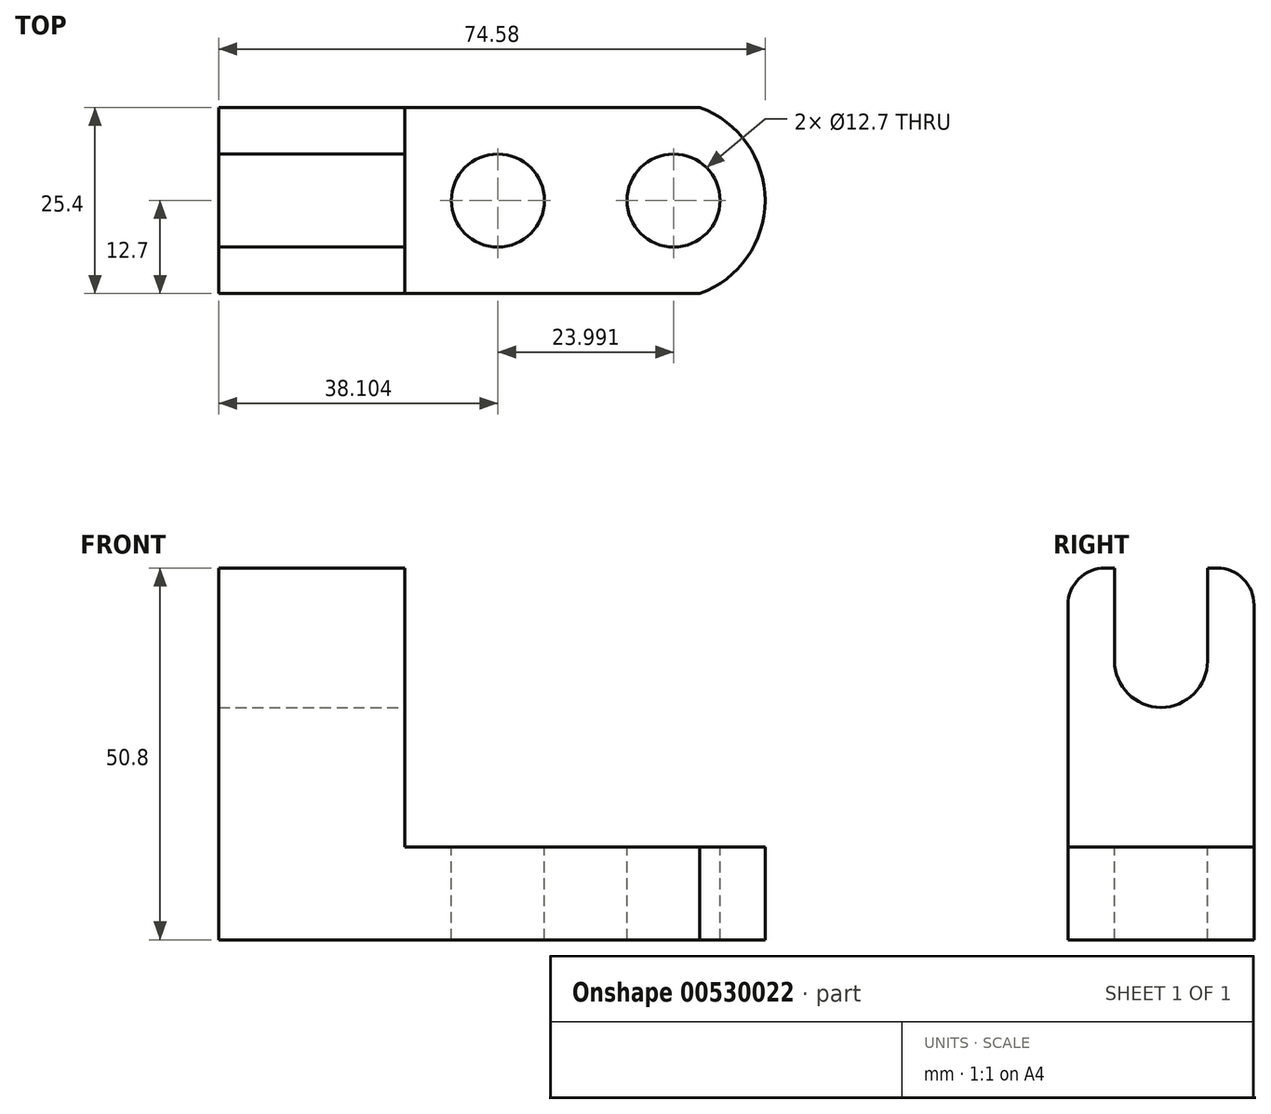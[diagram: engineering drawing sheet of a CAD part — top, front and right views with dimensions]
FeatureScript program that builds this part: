
annotation { "Feature Type Name" : "Feature", "Feature Type Description" : "" }
export const myFeature = defineFeature(function(context is Context, id is Id, definition is map)
    precondition{}
    {
        {
            var Q0;
            Q0=qCreatedBy(makeId("Front.planeOp"),FACE);
            var sketch = newSketch(context, id + "F0", { "sketchPlane" : qUnion([Q0])});
            skLineSegment(sketch, "E0", {"start": v(-65.68, 60.9) * mm, "end": v(-65.68, 10.1) * mm});
            skLineSegment(sketch, "E1", {"start": v(-65.68, 10.1) * mm, "end": v(9.11, 10.1) * mm});
            skLineSegment(sketch, "E2", {"start": v(9.11, 10.1) * mm, "end": v(9.11, 22.8) * mm});
            skLineSegment(sketch, "E3", {"start": v(9.11, 22.8) * mm, "end": v(-40.28, 22.8) * mm});
            skLineSegment(sketch, "E4", {"start": v(-40.28, 22.8) * mm, "end": v(-40.28, 60.9) * mm});
            skLineSegment(sketch, "E5", {"start": v(-65.68, 60.9) * mm, "end": v(-40.28, 60.9) * mm});
            skSolve(sketch);
        }
        {
            var Q0;
            Q0=makeQuery(id+"F0.imprint","IMPRINT",FACE,{"disambiguationData":[TD([[makeQuery(id+"F0.imprint","IMPRINT",EDGE,{"derivedFrom":sQuery(id+"F0.wireOp",EDGE,"E0")}),1.0]])]});
            extrude(context, id + "F1", {"entities" : qUnion([Q0]), "depth" : 25.4 * mm, "offsetDistance" : 25.4 * mm});
        }
        {
            var Q0;
            Q0=makeQuery(id+"F1.opExtrude","SWEPT_FACE",FACE,{"disambiguationData":[OSD([sQuery(id+"F0.wireOp",EDGE,"E3")])]});
            var sketch = newSketch(context, id + "F2", { "sketchPlane" : qUnion([Q0])});
            skCircle(sketch, "E6", {"center": v(-27.58, -12.7) * mm, "radius": 6.35 * mm});
            skCircle(sketch, "E7", {"center": v(-3.59, -12.7) * mm, "radius": 6.35 * mm});
            skArc(sketch, "E8", {"start": v(0, -25.4) * mm, "mid": v(8.9, -12.7) * mm, "end": v(0, 0) * mm});
            skSolve(sketch);
        }
        {
            var Q0;
            Q0=makeQuery(id+"F2.imprint","IMPRINT",FACE,{"disambiguationData":[TD([[makeQuery(id+"F2.imprint","IMPRINT",EDGE,{"derivedFrom":sQuery(id+"F2.wireOp",EDGE,"E6")}),1.0]])]});
            var Q1;
            Q1=makeQuery(id+"F2.imprint","IMPRINT",FACE,{"disambiguationData":[TD([[makeQuery(id+"F2.imprint","IMPRINT",EDGE,{"derivedFrom":sQuery(id+"F2.wireOp",EDGE,"E7")}),1.0]])]});
            var Q2;
            {var subQ0=sQuery(id+"F2.wireOp",EDGE,"E8");Q2=makeQuery(id+"F2.imprint","IMPRINT",FACE,{"disambiguationData":[TD([[makeQuery(id+"F2.imprint","IMPRINT",EDGE,{"derivedFrom":subQ0}),-1.0]])]});}
            extrude(context, id + "F3", {"entities" : qUnion([Q0, Q1, Q2]), "operationType" : NewBodyOperationType.REMOVE, "endBound" : BoundingType.THROUGH_ALL, "oppositeDirection" : true, "depth" : 25.4 * mm, "offsetDistance" : 25.4 * mm});
        }
        {
            var Q0;
            Q0=makeQuery(id+"F1.opExtrude","SWEPT_FACE",FACE,{"disambiguationData":[OSD([sQuery(id+"F0.wireOp",EDGE,"E4")])]});
            var sketch = newSketch(context, id + "F4", { "sketchPlane" : qUnion([Q0])});
            skCircle(sketch, "E9", {"center": v(-12.7, 48.2) * mm, "radius": 6.35 * mm});
            skLineSegment(sketch, "E10", {"start": v(-19.05, 48.2) * mm, "end": v(-19.05, 60.9) * mm});
            skLineSegment(sketch, "E11", {"start": v(-6.35, 48.2) * mm, "end": v(-6.35, 60.9) * mm});
            skLineSegment(sketch, "E12", {"start": v(-19.05, 60.9) * mm, "end": v(-25.4, 60.9) * mm});
            skLineSegment(sketch, "E13", {"start": v(-6.35, 60.9) * mm, "end": v(0, 60.9) * mm});
            skLineSegment(sketch, "E14", {"start": v(-19.05, 60.9) * mm, "end": v(-6.35, 60.9) * mm});
            skSolve(sketch);
        }
        {
            var Q0;
            {var subQ0=sQuery(id+"F4.wireOp",EDGE,"E9");var subQ1=makeQuery(id+"F4.imprint","INTERSECT",VERTEX,{"derivedFrom":[subQ0,sQuery(id+"F4.wireOp",EDGE,"E10")]});Q0=makeQuery(id+"F4.imprint","IMPRINT",FACE,{"disambiguationData":[TD([[makeQuery(id+"F4.imprint","IMPRINT",EDGE,{"disambiguationData":[TD([[subQ1,1.0]])],"derivedFrom":subQ0}),1.0]])]});}
            var Q1;
            {var subQ0=sQuery(id+"F4.wireOp",EDGE,"E10");Q1=makeQuery(id+"F4.imprint","IMPRINT",FACE,{"disambiguationData":[TD([[makeQuery(id+"F4.imprint","IMPRINT",EDGE,{"derivedFrom":subQ0}),-1.0]])]});}
            extrude(context, id + "F5", {"entities" : qUnion([Q0, Q1]), "operationType" : NewBodyOperationType.REMOVE, "endBound" : BoundingType.THROUGH_ALL, "oppositeDirection" : true, "depth" : 25.4 * mm, "offsetDistance" : 25.4 * mm});
        }
        {
            var Q0;
            Q0=makeQuery(id+"F1.opExtrude","CAP_EDGE",EDGE,{"disambiguationData":[OSD([sQuery(id+"F0.wireOp",EDGE,"E5")])],"isStart":false});
            fillet(context, id + "F6", {"entities" : qUnion([Q0]), "radius" : 5.08 * mm, "tangentPropagation" : true, "allowEdgeOverflow" : false});
        }
        {
            var Q0;
            Q0=makeQuery(id+"F1.opExtrude","CAP_EDGE",EDGE,{"disambiguationData":[OSD([sQuery(id+"F0.wireOp",EDGE,"E5")])],"isStart":true});
            fillet(context, id + "F7", {"entities" : qUnion([Q0]), "radius" : 5.08 * mm, "tangentPropagation" : true, "allowEdgeOverflow" : false});
        }
    });
